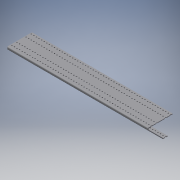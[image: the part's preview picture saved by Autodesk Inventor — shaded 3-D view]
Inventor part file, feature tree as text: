
AUTODESK INVENTOR PART (.ipt)
format: ipt  version: 2016 (Build 200138000, 138)  size: 584,704 bytes
history: native  units: in
note: dims shown in document units (in); Inventor stores cm internally (conversion verified against a paired STEP export)
features: extrude x2, sketch x2, other x1
ambient origin geometry x8: Origin, YZ Plane, XZ Plane, XY Plane, X Axis, Y Axis, Z Axis, Center Point
bodies: Solid1 (feature_tree)
feature tree (5):
  extrude  "Extrusion1"  Depth=0.25in TaperAngle=0.0deg
  extrude  "Extrusion2"  [1 undecoded]
  sketch  "Sketch1"  dims[d0=3.75in d1=0.0in d2=0.25in d3=0.0in]
  sketch  "Sketch2"
  other  "LPattern2"
note: 1 required parameter value undecoded (feature->parameter linkage not recoverable at this tier; creation-order binding heuristic only, values carry confidence <= 0.55)
